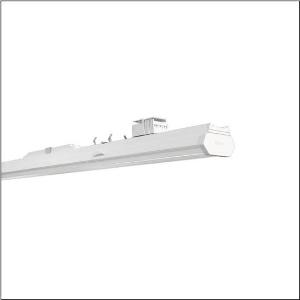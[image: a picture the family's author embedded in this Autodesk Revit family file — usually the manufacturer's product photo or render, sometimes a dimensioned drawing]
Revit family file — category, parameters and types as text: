
# Revit family: licross_r__11_protected_ho_51td11dn4f5s_b27d
name_source: partatom
category: Lighting Fixtures
units: mm (PartAtom-declared; Revit-internal decimal feet)

## family parameters
Cut with Voids When Loaded = No
Host = Face
Light Source = No
Part Type = Normal
Room Calculation Point = No
Round Connector Dimension = Use Diameter
Shared = No

## types (1)
- --- (1 x LED, 15510 lm, 87.3 W, 4000K)
    Apparent Load = 87 VA
    CIE Flux Codes = 84 94 98 99 100
    Color Rendering = 80
    Color Temperature = 4000K
    Default Elevation = 1800 mm
    Description = Licross® 11 Protected HO, luminaire insert, of sheet steel, galvanised, coil coated, white, length: 1.500mm, width: 90mm, height: 101mm, LED rated luminous flux: 15.510lm, light colour: 840, control gear: DALI 2, with plug, 5-pole, with phase selection, mains connection: 220..240V, AC, 50/60Hz, rated input power: 87W, halogen-free wiring, primary light control with lens, of plastic, primary optical cover: cover, of PMMA, light emission: direct distribution, primary light characteristic: symmetric, protection rating (complete): IP54, insulation class (complete): insulation class I (protective earthing), certification: CE, ENEC, VDE, UKCA, protection symbol: D if used in an environment with non-conductive dust loads with corresponding accessories, impact resistance: IK06, permissible ambient temperature for indoor applications: -25..+30°C, corresponds to IFS (International Featured Standards) requirements for safety and quality in the food industry, reducing of maximum allowable ambient temperature of 5°C with ceiling mounting, LABS conformity tested according to VDMA 24364:2018-05, packaging unit: 1 piece
    Height = 92 mm
    Lamp = 1 x LED
    Lamp Light Flux = 15510 lm
    Lamp Power = 87.3 W
    Lamp count = 1
    Length = 1500 mm
    Luminous efficacy = 178 lm/W
    Manufacturer = Siteco
    ModVariant = No
    Model = 51TD11DN4F5S
    Mounting Place = Ceiling
    Mounting Type = Pendant
    Number of Poles = 1
    OnlyDefault = Yes
    Power Factor = 1
    Product Name = Licross® 11 Protected HO
    Product group = luminaire insert
    ProductGroupID = 901
    Protection Class = Protection class I
    Protection Degree = IP 54
    RLX_Detail_Level = 1
    RLX_Emergency_Light_Flux = 0 lm
    RLX_Emergency_Type = 0
    RLX_Emergency_Type_DB = No
    RlxData = <blob elided: 24377 chars, md5=42b7a894>
    Socket = socket
    Standby Power = 0 W
    System Light Flux = 15510 lm
    System Power = 87 W
    Type Comments = factory setting: luminous flux: 100 % | dim-lin: 254 | 589 mA
    Type Image = l_1256145.jpg
    URL = http://relux.com
    VarID = @adj_031183
    Voltage = 0 V
    Weight = 0.00 kg
    Width = 88 mm

## geometry (parser evidence)
native form markers: Blend x4, Sweep x11
no freeform markers — native parametric forms only
